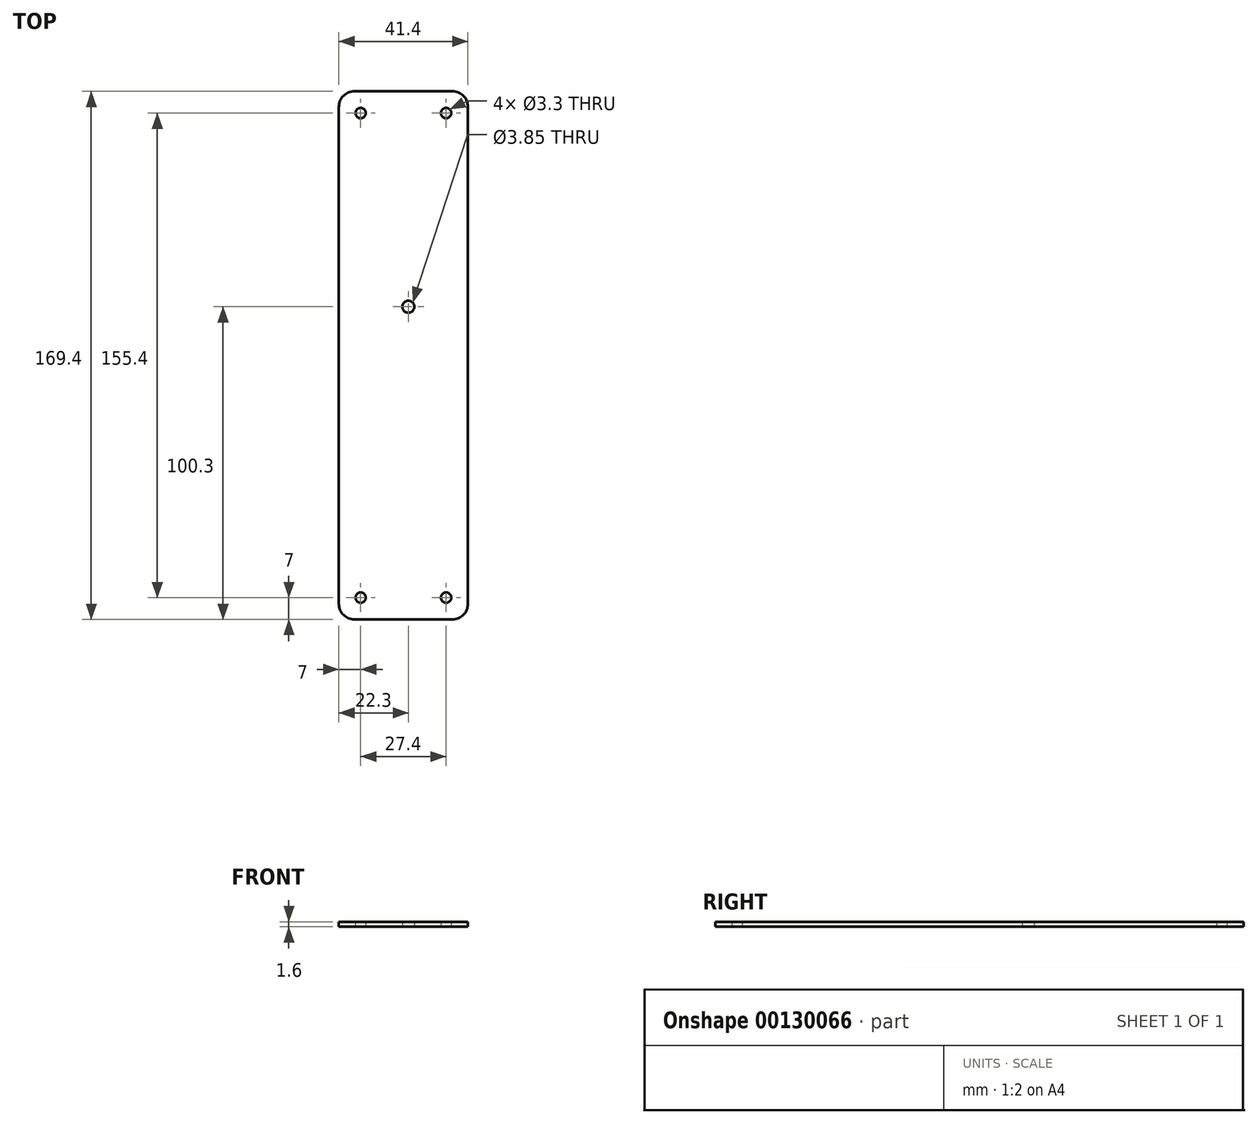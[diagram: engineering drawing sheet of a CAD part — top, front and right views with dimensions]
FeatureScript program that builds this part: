
annotation { "Feature Type Name" : "Feature", "Feature Type Description" : "" }
export const myFeature = defineFeature(function(context is Context, id is Id, definition is map)
    precondition{}
    {
        {
            var Q0;
            Q0=qCreatedBy(makeId("Top.planeOp"),FACE);
            var sketch = newSketch(context, id + "F0", { "sketchPlane" : qUnion([Q0])});
            skLineSegment(sketch, "E0.bottom", {"start": v(13.7, 77.7) * mm, "end": v(-13.7, 77.7) * mm});
            skLineSegment(sketch, "E0.top", {"start": v(13.7, -77.7) * mm, "end": v(-13.7, -77.7) * mm});
            skLineSegment(sketch, "E0.left", {"start": v(13.7, 77.7) * mm, "end": v(13.7, -77.7) * mm});
            skLineSegment(sketch, "E0.right", {"start": v(-13.7, 77.7) * mm, "end": v(-13.7, -77.7) * mm});
            skPoint(sketch, "E0.middle", {"position": v(0, 0) * mm});
            skCircle(sketch, "E1", {"center": v(1.6, 15.6) * mm, "radius": 1.92 * mm});
            skCircle(sketch, "E2", {"center": v(13.7, 77.7) * mm, "radius": 1.65 * mm});
            skCircle(sketch, "E3", {"center": v(-13.7, 77.7) * mm, "radius": 1.65 * mm});
            skCircle(sketch, "E4", {"center": v(13.7, -77.7) * mm, "radius": 1.65 * mm});
            skCircle(sketch, "E5", {"center": v(-13.7, -77.7) * mm, "radius": 1.65 * mm});
            skLineSegment(sketch, "E6.bottom", {"start": v(-20.7, 84.7) * mm, "end": v(20.7, 84.7) * mm});
            skLineSegment(sketch, "E6.top", {"start": v(-20.7, -84.7) * mm, "end": v(20.7, -84.7) * mm});
            skLineSegment(sketch, "E6.left", {"start": v(-20.7, 84.7) * mm, "end": v(-20.7, -84.7) * mm});
            skLineSegment(sketch, "E6.right", {"start": v(20.7, 84.7) * mm, "end": v(20.7, -84.7) * mm});
            skSolve(sketch);
        }
        {
            var Q0;
            Q0=makeQuery(id+"F0.imprint","IMPRINT",FACE,{"disambiguationData":[TD([[makeQuery(id+"F0.imprint","IMPRINT",EDGE,{"derivedFrom":sQuery(id+"F0.wireOp",EDGE,"E6.bottom")}),-1.0]])]});
            var Q1;
            Q1=makeQuery(id+"F0.imprint","IMPRINT",FACE,{"disambiguationData":[TD([[makeQuery(id+"F0.imprint","IMPRINT",EDGE,{"derivedFrom":sQuery(id+"F0.wireOp",EDGE,"E1")}),-1.0]])]});
            extrude(context, id + "F1", {"entities" : qUnion([Q0, Q1]), "depth" : 1.6 * mm});
        }
        {
            var Q0;
            Q0=makeQuery(id+"F1.opExtrude","SWEPT_EDGE",EDGE,{"disambiguationData":[OSD([sQuery(id+"F0.wireOp",EDGE,"E6.top"),sQuery(id+"F0.wireOp",EDGE,"E6.left")])]});
            var Q1;
            Q1=makeQuery(id+"F1.opExtrude","SWEPT_EDGE",EDGE,{"disambiguationData":[OSD([sQuery(id+"F0.wireOp",EDGE,"E6.top"),sQuery(id+"F0.wireOp",EDGE,"E6.right")])]});
            var Q2;
            Q2=makeQuery(id+"F1.opExtrude","SWEPT_EDGE",EDGE,{"disambiguationData":[OSD([sQuery(id+"F0.wireOp",EDGE,"E6.bottom"),sQuery(id+"F0.wireOp",EDGE,"E6.right")])]});
            var Q3;
            Q3=makeQuery(id+"F1.opExtrude","SWEPT_EDGE",EDGE,{"disambiguationData":[OSD([sQuery(id+"F0.wireOp",EDGE,"E6.bottom"),sQuery(id+"F0.wireOp",EDGE,"E6.left")])]});
            fillet(context, id + "F2", {"entities" : qUnion([Q0, Q1, Q2, Q3]), "radius" : 5 * mm, "tangentPropagation" : true, "allowEdgeOverflow" : false});
        }
    });
